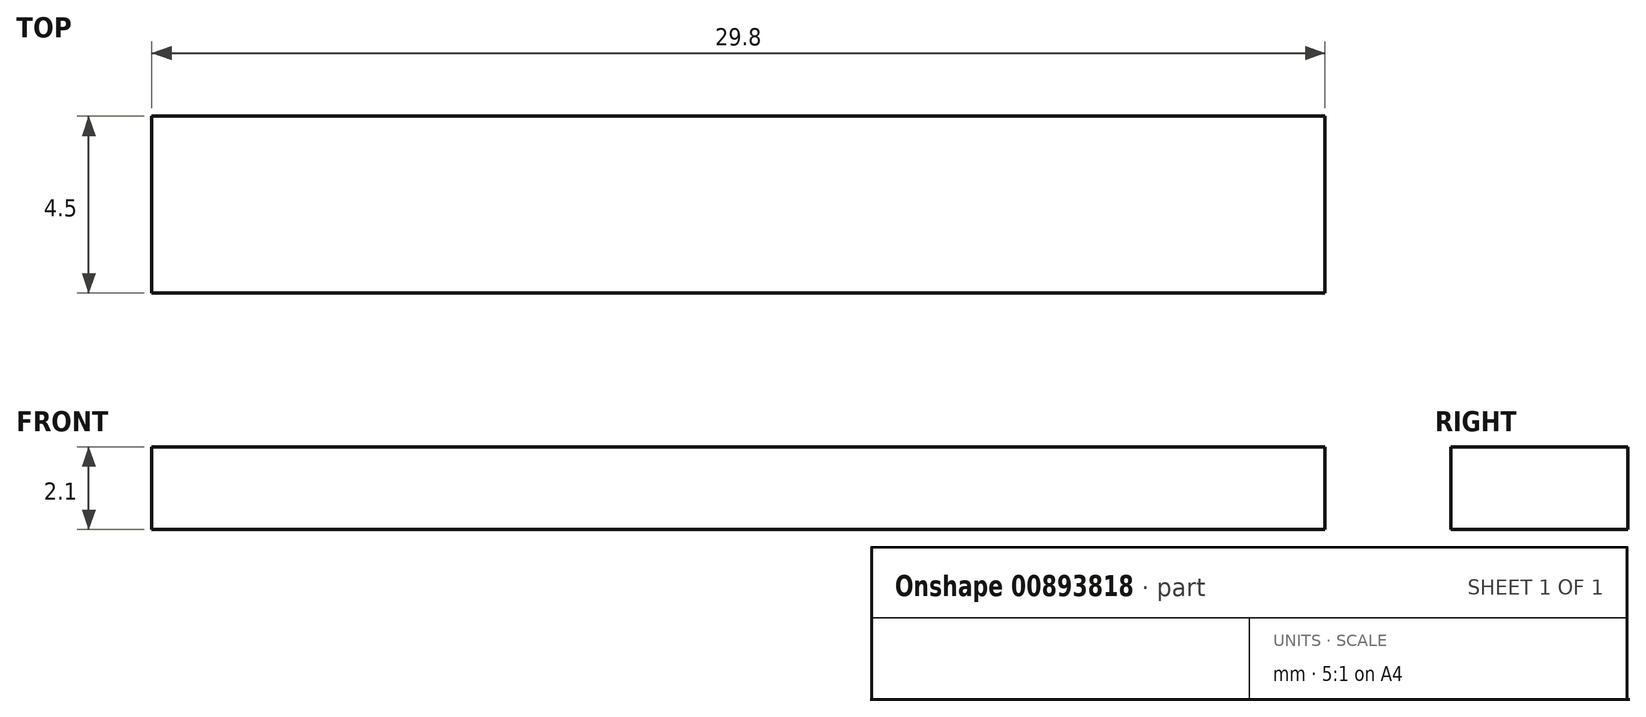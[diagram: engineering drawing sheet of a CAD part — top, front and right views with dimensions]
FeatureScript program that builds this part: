
annotation { "Feature Type Name" : "Feature", "Feature Type Description" : "" }
export const myFeature = defineFeature(function(context is Context, id is Id, definition is map)
    precondition{}
    {
        {
            var Q0;
            Q0=qCreatedBy(makeId("Front.planeOp"),FACE);
            var sketch = newSketch(context, id + "F0", { "sketchPlane" : qUnion([Q0])});
            skLineSegment(sketch, "E0", {"start": v(-44.13, 0) * mm, "end": v(-14.33, 0) * mm});
            skSolve(sketch);
        }
        {
            var Q0;
            Q0=sQuery(id+"F0.wireOp",EDGE,"E0");
            extrude(context, id + "F1", {"bodyType" : ToolBodyType.SURFACE, "surfaceEntities" : qUnion([Q0]), "oppositeDirection" : true, "depth" : 4.5 * mm, "offsetDistance" : 25 * mm});
        }
        {
            var Q0;
            Q0=makeQuery(id+"F1.opExtrude","SWEPT_FACE",FACE,{"disambiguationData":[OSD([sQuery(id+"F0.wireOp",EDGE,"E0")])]});
            extrude(context, id + "F2", {"entities" : qUnion([Q0]), "oppositeDirection" : true, "depth" : 2.1 * mm, "offsetDistance" : 25 * mm});
        }
    });
